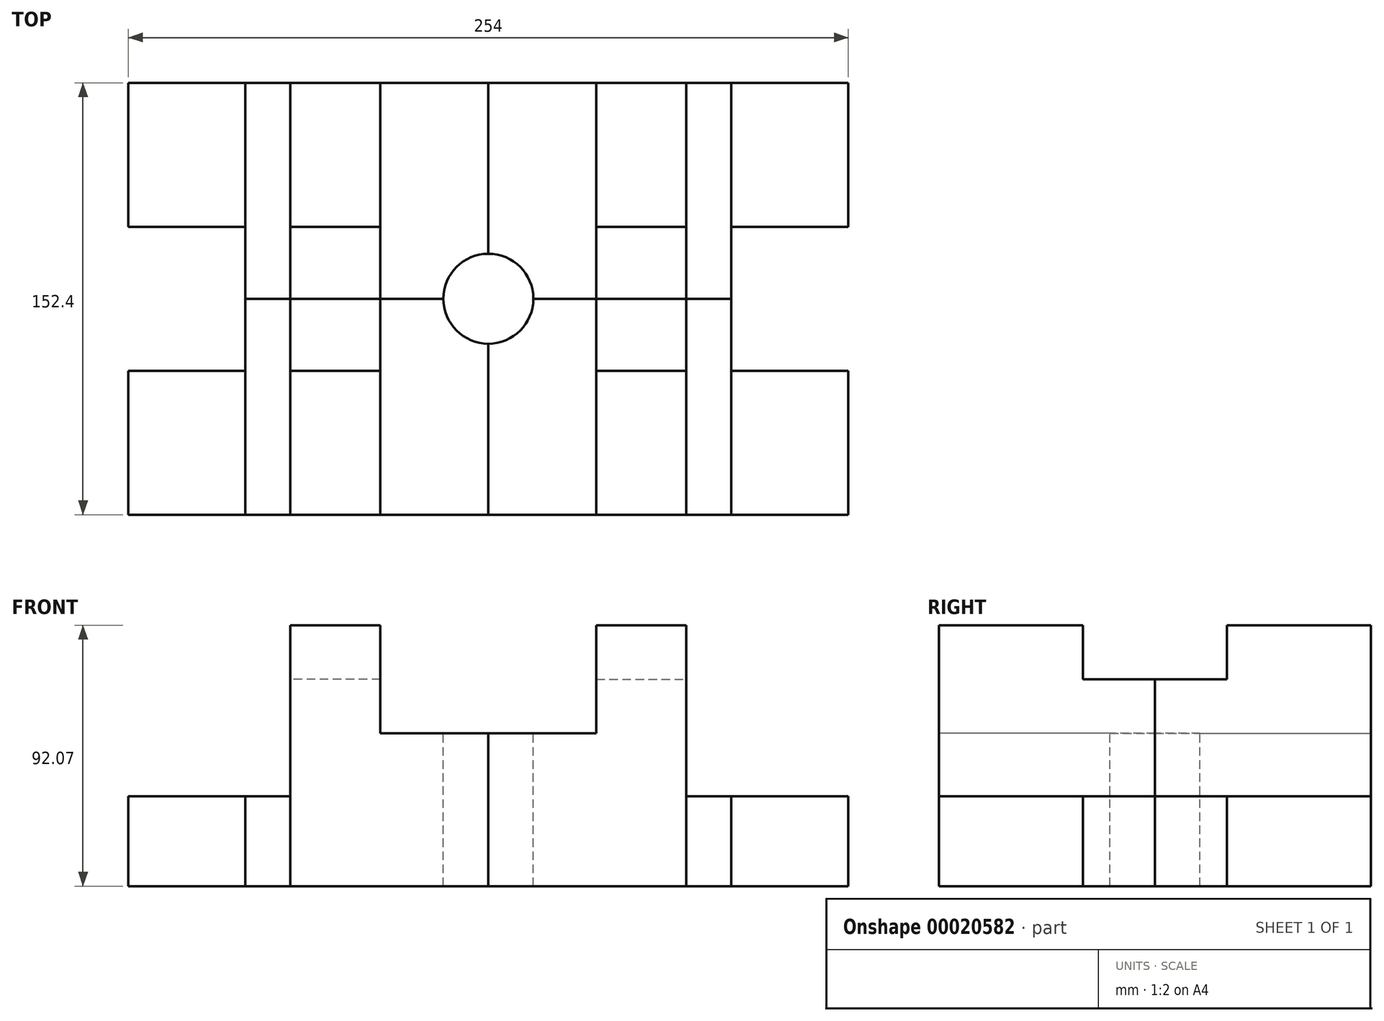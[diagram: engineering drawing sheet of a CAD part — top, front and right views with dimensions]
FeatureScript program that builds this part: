
annotation { "Feature Type Name" : "Feature", "Feature Type Description" : "" }
export const myFeature = defineFeature(function(context is Context, id is Id, definition is map)
    precondition{}
    {
        {
            var Q0;
            Q0=qCreatedBy(makeId("Front.planeOp"),FACE);
            var sketch = newSketch(context, id + "F0", { "sketchPlane" : qUnion([Q0])});
            skLineSegment(sketch, "E0", {"start": v(-102.65, 22.22) * mm, "end": v(-102.65, -31.75) * mm});
            skLineSegment(sketch, "E1", {"start": v(-102.65, -31.75) * mm, "end": v(-16.92, -31.75) * mm});
            skLineSegment(sketch, "E2", {"start": v(-102.65, 22.22) * mm, "end": v(-64.55, 22.23) * mm});
            skLineSegment(sketch, "E3", {"start": v(-64.55, 22.23) * mm, "end": v(-64.55, 60.33) * mm});
            skLineSegment(sketch, "E4", {"start": v(-64.55, 60.33) * mm, "end": v(-32.8, 60.33) * mm});
            skLineSegment(sketch, "E5", {"start": v(-32.8, 60.33) * mm, "end": v(-32.8, 0) * mm});
            skLineSegment(sketch, "E6", {"start": v(-32.8, 0) * mm, "end": v(-16.92, 0) * mm});
            skLineSegment(sketch, "E7", {"start": v(24.35, -31.75) * mm, "end": v(24.35, 0) * mm});
            skLineSegment(sketch, "E8", {"start": v(-16.92, 0) * mm, "end": v(-16.92, -31.75) * mm});
            skLineSegment(sketch, "E9", {"start": v(-16.92, 0) * mm, "end": v(24.35, 0) * mm});
            skLineSegment(sketch, "E10", {"start": v(-16.92, -31.75) * mm, "end": v(24.35, -31.75) * mm});
            skLineSegment(sketch, "E11", {"start": v(-32.8, 0) * mm, "end": v(-32.8, -31.75) * mm});
            skSolve(sketch);
        }
        {
            var Q0;
            {var subQ2=sQuery(id+"F0.wireOp",EDGE,"E0");Q0=makeQuery(id+"F0.imprint","IMPRINT",FACE,{"disambiguationData":[TD([[makeQuery(id+"F0.imprint","IMPRINT",EDGE,{"derivedFrom":subQ2}),1.0]])]});}
            extrude(context, id + "F1", {"entities" : qUnion([Q0]), "oppositeDirection" : true, "depth" : 76.2 * mm});
        }
        {
            var Q0;
            Q0=makeQuery(id+"F0.imprint","IMPRINT",FACE,{"disambiguationData":[TD([[makeQuery(id+"F0.imprint","IMPRINT",EDGE,{"derivedFrom":sQuery(id+"F0.wireOp",EDGE,"E6")}),-1.0]])]});
            extrude(context, id + "F2", {"entities" : qUnion([Q0]), "oppositeDirection" : true, "depth" : 76.2 * mm});
        }
        {
            var Q0;
            Q0=makeQuery(id+"F0.imprint","IMPRINT",FACE,{"disambiguationData":[TD([[makeQuery(id+"F0.imprint","IMPRINT",EDGE,{"derivedFrom":sQuery(id+"F0.wireOp",EDGE,"E7")}),1.0]])]});
            extrude(context, id + "F3", {"entities" : qUnion([Q0]), "oppositeDirection" : true, "depth" : 50.8 * mm});
        }
        {
            var Q0;
            Q0=makeQuery(id+"F1.opExtrude","SWEPT_FACE",FACE,{"disambiguationData":[OSD([sQuery(id+"F0.wireOp",EDGE,"E4")])]});
            var sketch = newSketch(context, id + "F4", { "sketchPlane" : qUnion([Q0])});
            skLineSegment(sketch, "E12", {"start": v(-64.55, 50.8) * mm, "end": v(-32.8, 50.8) * mm});
            skLineSegment(sketch, "E13", {"start": v(-64.55, 76.2) * mm, "end": v(-64.55, 50.8) * mm});
            skLineSegment(sketch, "E14", {"start": v(-32.8, 76.2) * mm, "end": v(-32.8, 50.8) * mm});
            skLineSegment(sketch, "E15", {"start": v(-64.55, 50.8) * mm, "end": v(-64.55, 0) * mm});
            skLineSegment(sketch, "E16", {"start": v(-32.8, 50.8) * mm, "end": v(-32.8, 0) * mm});
            skSolve(sketch);
        }
        {
            var Q0;
            Q0=makeQuery(id+"F4.imprint","IMPRINT",FACE,{"disambiguationData":[TD([[makeQuery(id+"F4.imprint","IMPRINT",EDGE,{"derivedFrom":sQuery(id+"F4.wireOp",EDGE,"E12")}),1.0]])]});
            extrude(context, id + "F5", {"entities" : qUnion([Q0]), "operationType" : NewBodyOperationType.REMOVE, "oppositeDirection" : true, "depth" : 19.05 * mm});
        }
        {
            var Q0;
            Q0=makeQuery(id+"F1.opExtrude","SWEPT_FACE",FACE,{"disambiguationData":[OSD([sQuery(id+"F0.wireOp",EDGE,"E2")])]});
            var sketch = newSketch(context, id + "F6", { "sketchPlane" : qUnion([Q0])});
            skArc(sketch, "E17", {"start": v(-102.9, 60.33) * mm, "mid": v(-91.4, 64.99) * mm, "end": v(-86.78, 76.5) * mm});
            skSolve(sketch);
        }
        {
            var Q0;
            {var subQ0=sQuery(id+"F0.wireOp",EDGE,"E2");var subQ1=makeQuery(id+"F1.opExtrude","CAP_EDGE",EDGE,{"disambiguationData":[OSD([subQ0])],"isStart":false});var subQ2=sQuery(id+"F6.wireOp",EDGE,"E17");var subQ3=makeQuery(id+"F6.imprint","INTERSECT",VERTEX,{"derivedFrom":[subQ1,subQ2]});Q0=makeQuery(id+"F6.imprint","IMPRINT",FACE,{"disambiguationData":[TD([[makeQuery(id+"F6.imprint","IMPRINT",EDGE,{"disambiguationData":[TD([[subQ3,1.0]])],"derivedFrom":subQ2}),1.0]])]});}
            extrude(context, id + "F7", {"entities" : qUnion([Q0]), "operationType" : NewBodyOperationType.REMOVE, "endBound" : BoundingType.THROUGH_ALL, "oppositeDirection" : true, "depth" : 25.4 * mm});
        }
        {
            var Q0;
            Q0=makeQuery(id+"F1.opExtrude","SWEPT_BODY",BODY,{"disambiguationData":[OSD([sQuery(id+"F0.wireOp",EDGE,"E0"),sQuery(id+"F0.wireOp",EDGE,"E1"),sQuery(id+"F0.wireOp",EDGE,"E2"),sQuery(id+"F0.wireOp",EDGE,"E3"),sQuery(id+"F0.wireOp",EDGE,"E4"),sQuery(id+"F0.wireOp",EDGE,"E5"),sQuery(id+"F0.wireOp",EDGE,"E11")])]});
            var Q1;
            Q1=makeQuery(id+"F2.opExtrude","SWEPT_BODY",BODY,{"disambiguationData":[OSD([sQuery(id+"F0.wireOp",EDGE,"E1"),sQuery(id+"F0.wireOp",EDGE,"E6"),sQuery(id+"F0.wireOp",EDGE,"E8"),sQuery(id+"F0.wireOp",EDGE,"E11")])]});
            var Q2;
            Q2=makeQuery(id+"F3.opExtrude","SWEPT_BODY",BODY,{"disambiguationData":[OSD([sQuery(id+"F0.wireOp",EDGE,"E7"),sQuery(id+"F0.wireOp",EDGE,"E8"),sQuery(id+"F0.wireOp",EDGE,"E9"),sQuery(id+"F0.wireOp",EDGE,"E10")])]});
            var Q3;
            Q3=makeQuery(id+"F1.opExtrude","CAP_FACE",FACE,{"disambiguationData":[OSD([sQuery(id+"F0.wireOp",EDGE,"E0"),sQuery(id+"F0.wireOp",EDGE,"E1"),sQuery(id+"F0.wireOp",EDGE,"E2"),sQuery(id+"F0.wireOp",EDGE,"E3"),sQuery(id+"F0.wireOp",EDGE,"E4"),sQuery(id+"F0.wireOp",EDGE,"E5"),sQuery(id+"F0.wireOp",EDGE,"E11")])],"isStart":false});
            mirror(context, id + "F8", {"entities" : qUnion([Q0, Q1, Q2]), "mirrorPlane" : qUnion([Q3])});
        }
        {
            var Q0;
            Q0=makeQuery(id+"F8.opPattern","COPY",BODY,{"derivedFrom":makeQuery(id+"F1.opExtrude","SWEPT_BODY",BODY,{"disambiguationData":[OSD([sQuery(id+"F0.wireOp",EDGE,"E0"),sQuery(id+"F0.wireOp",EDGE,"E1"),sQuery(id+"F0.wireOp",EDGE,"E2"),sQuery(id+"F0.wireOp",EDGE,"E3"),sQuery(id+"F0.wireOp",EDGE,"E4"),sQuery(id+"F0.wireOp",EDGE,"E5"),sQuery(id+"F0.wireOp",EDGE,"E11")])]}),"instanceName":"1"});
            var Q1;
            Q1=makeQuery(id+"F1.opExtrude","SWEPT_BODY",BODY,{"disambiguationData":[OSD([sQuery(id+"F0.wireOp",EDGE,"E0"),sQuery(id+"F0.wireOp",EDGE,"E1"),sQuery(id+"F0.wireOp",EDGE,"E2"),sQuery(id+"F0.wireOp",EDGE,"E3"),sQuery(id+"F0.wireOp",EDGE,"E4"),sQuery(id+"F0.wireOp",EDGE,"E5"),sQuery(id+"F0.wireOp",EDGE,"E11")])]});
            var Q2;
            Q2=makeQuery(id+"F2.opExtrude","SWEPT_BODY",BODY,{"disambiguationData":[OSD([sQuery(id+"F0.wireOp",EDGE,"E1"),sQuery(id+"F0.wireOp",EDGE,"E6"),sQuery(id+"F0.wireOp",EDGE,"E8"),sQuery(id+"F0.wireOp",EDGE,"E11")])]});
            var Q3;
            Q3=makeQuery(id+"F8.opPattern","COPY",BODY,{"derivedFrom":makeQuery(id+"F2.opExtrude","SWEPT_BODY",BODY,{"disambiguationData":[OSD([sQuery(id+"F0.wireOp",EDGE,"E1"),sQuery(id+"F0.wireOp",EDGE,"E6"),sQuery(id+"F0.wireOp",EDGE,"E8"),sQuery(id+"F0.wireOp",EDGE,"E11")])]}),"instanceName":"1"});
            var Q4;
            Q4=makeQuery(id+"F8.opPattern","COPY",BODY,{"derivedFrom":makeQuery(id+"F3.opExtrude","SWEPT_BODY",BODY,{"disambiguationData":[OSD([sQuery(id+"F0.wireOp",EDGE,"E7"),sQuery(id+"F0.wireOp",EDGE,"E8"),sQuery(id+"F0.wireOp",EDGE,"E9"),sQuery(id+"F0.wireOp",EDGE,"E10")])]}),"instanceName":"1"});
            var Q5;
            Q5=makeQuery(id+"F3.opExtrude","SWEPT_BODY",BODY,{"disambiguationData":[OSD([sQuery(id+"F0.wireOp",EDGE,"E7"),sQuery(id+"F0.wireOp",EDGE,"E8"),sQuery(id+"F0.wireOp",EDGE,"E9"),sQuery(id+"F0.wireOp",EDGE,"E10")])]});
            var Q6;
            Q6=makeQuery(id+"F8.opPattern","COPY",FACE,{"derivedFrom":makeQuery(id+"F1.opExtrude","SWEPT_FACE",FACE,{"disambiguationData":[OSD([sQuery(id+"F0.wireOp",EDGE,"E0")])]}),"instanceName":"1"});
            mirror(context, id + "F9", {"entities" : qUnion([Q0, Q1, Q2, Q3, Q4, Q5]), "mirrorPlane" : qUnion([Q6])});
        }
    });
